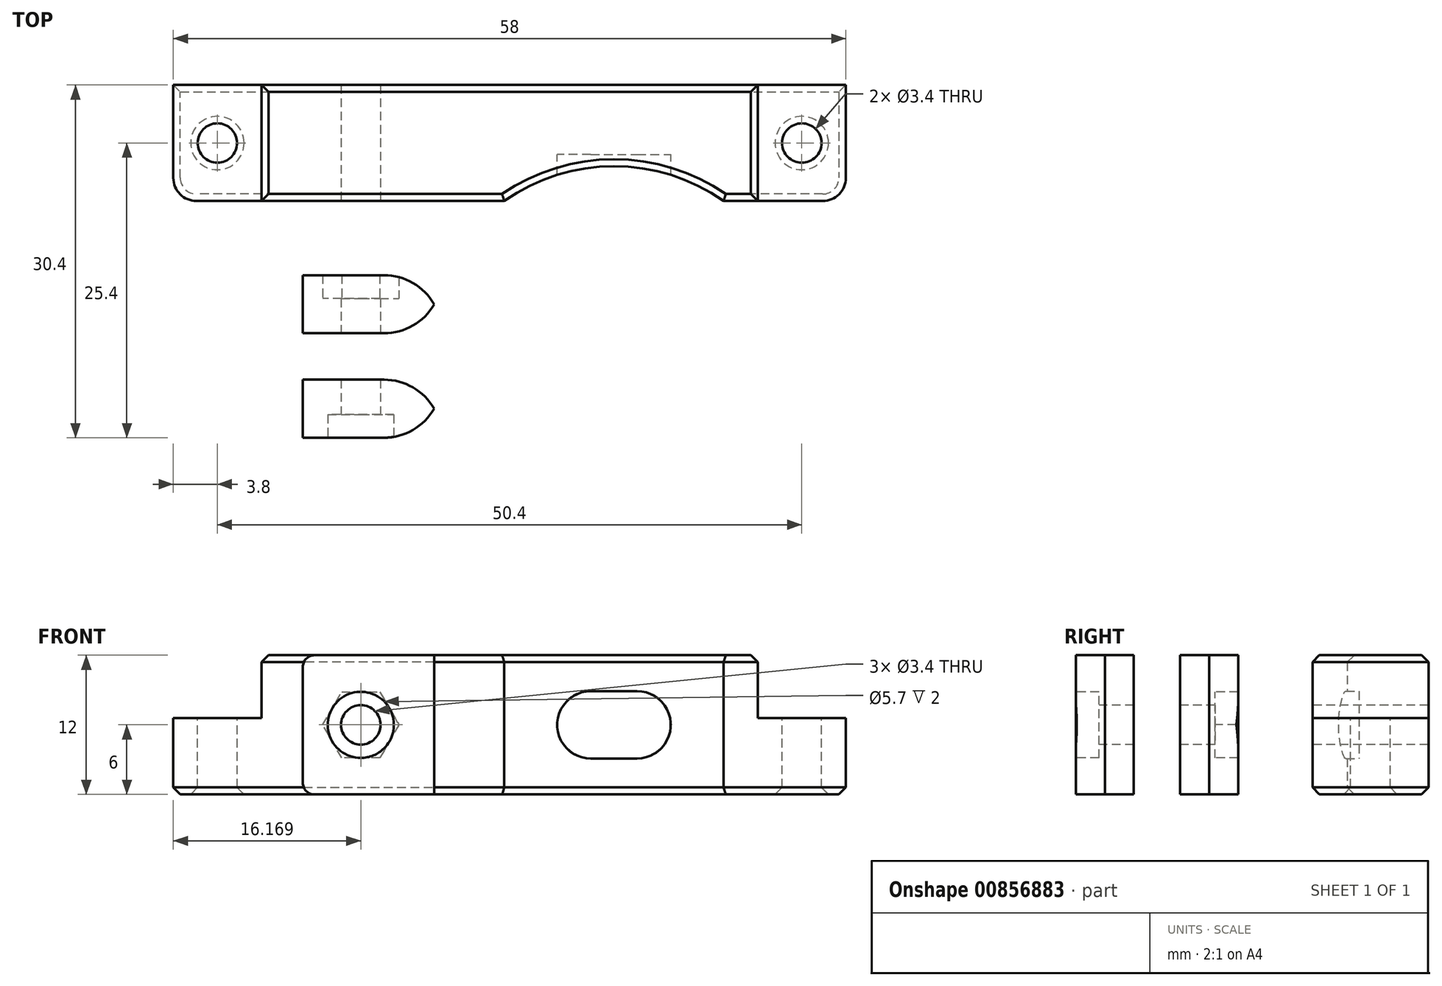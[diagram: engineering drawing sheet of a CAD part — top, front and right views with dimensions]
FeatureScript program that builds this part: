
annotation { "Feature Type Name" : "Feature", "Feature Type Description" : "" }
export const myFeature = defineFeature(function(context is Context, id is Id, definition is map)
    precondition{}
    {
        {
            var Q0;
            Q0=qCreatedBy(makeId("Top.planeOp"),FACE);
            var sketch = newSketch(context, id + "F0", { "sketchPlane" : qUnion([Q0])});
            skLineSegment(sketch, "E0.bottom", {"start": v(29, -5) * mm, "end": v(-29, -5) * mm});
            skLineSegment(sketch, "E0.top", {"start": v(29, 5) * mm, "end": v(-29, 5) * mm});
            skLineSegment(sketch, "E0.left", {"start": v(29, -5) * mm, "end": v(29, 5) * mm});
            skLineSegment(sketch, "E0.right", {"start": v(-29, -5) * mm, "end": v(-29, 5) * mm});
            skPoint(sketch, "E0.middle", {"position": v(0, 0) * mm});
            skCircle(sketch, "E1", {"center": v(9, -18.4) * mm, "radius": 13.4 * mm});
            skCircle(sketch, "E2", {"center": v(9, -18.4) * mm, "radius": 16.4 * mm});
            skLineSegment(sketch, "E3", {"start": v(-7.4, -18.4) * mm, "end": v(25.4, -18.4) * mm, "construction": true});
            skLineSegment(sketch, "E4", {"start": v(-7.28, -16.4) * mm, "end": v(-4.25, -16.4) * mm});
            skLineSegment(sketch, "E5.MirrorCS", {"start": v(-7.28, -20.4) * mm, "end": v(-4.25, -20.4) * mm});
            skLineSegment(sketch, "E6.bottom", {"start": v(-17.83, -16.4) * mm, "end": v(-5.83, -16.4) * mm});
            skLineSegment(sketch, "E6.top", {"start": v(-17.83, -11.4) * mm, "end": v(-5.83, -11.4) * mm});
            skLineSegment(sketch, "E6.left", {"start": v(-17.83, -16.4) * mm, "end": v(-17.83, -11.4) * mm});
            skLineSegment(sketch, "E6.right", {"start": v(-5.83, -16.4) * mm, "end": v(-5.83, -11.4) * mm});
            skLineSegment(sketch, "E7.MirrorCS", {"start": v(-17.83, -20.4) * mm, "end": v(-5.83, -20.4) * mm});
            skLineSegment(sketch, "E8.MirrorCS", {"start": v(-5.83, -20.4) * mm, "end": v(-5.83, -25.4) * mm});
            skLineSegment(sketch, "E9.MirrorCS", {"start": v(-17.83, -25.4) * mm, "end": v(-5.83, -25.4) * mm});
            skLineSegment(sketch, "E10.MirrorCS", {"start": v(-17.83, -20.4) * mm, "end": v(-17.83, -25.4) * mm});
            skSolve(sketch);
        }
        {
            var Q0;
            {var subQ5=sQuery(id+"F0.wireOp",EDGE,"E5.MirrorCS");Q0=makeQuery(id+"F0.imprint","IMPRINT",FACE,{"disambiguationData":[TD([[makeQuery(id+"F0.imprint","IMPRINT",EDGE,{"derivedFrom":subQ5}),-1.0]])]});}
            var Q1;
            {var subQ5=sQuery(id+"F0.wireOp",EDGE,"E4");Q1=makeQuery(id+"F0.imprint","IMPRINT",FACE,{"disambiguationData":[TD([[makeQuery(id+"F0.imprint","IMPRINT",EDGE,{"derivedFrom":subQ5}),1.0]])]});}
            var Q2;
            {var subQ0=sQuery(id+"F0.wireOp",EDGE,"E2");var subQ1=sQuery(id+"F0.wireOp",EDGE,"E0.bottom");var subQ2=makeQuery(id+"F0.imprint","INTERSECT",VERTEX,{"disambiguationData":[OD(0.0)],"derivedFrom":[subQ1,subQ0]});Q2=makeQuery(id+"F0.imprint","IMPRINT",FACE,{"disambiguationData":[TD([[makeQuery(id+"F0.imprint","IMPRINT",EDGE,{"disambiguationData":[TD([[subQ2,-1.0]])],"derivedFrom":subQ1}),-1.0]])]});}
            var Q3;
            Q3=makeQuery(id+"F0.imprint","IMPRINT",FACE,{"disambiguationData":[TD([[makeQuery(id+"F0.imprint","IMPRINT",EDGE,{"derivedFrom":sQuery(id+"F0.wireOp",EDGE,"E0.top")}),1.0]])]});
            var Q4;
            {var subQ0=sQuery(id+"F0.wireOp",EDGE,"E6.top");Q4=makeQuery(id+"F0.imprint","IMPRINT",FACE,{"disambiguationData":[TD([[makeQuery(id+"F0.imprint","IMPRINT",EDGE,{"derivedFrom":subQ0}),-1.0]])]});}
            var Q5;
            {var subQ0=sQuery(id+"F0.wireOp",EDGE,"E6.right");Q5=makeQuery(id+"F0.imprint","IMPRINT",FACE,{"disambiguationData":[TD([[makeQuery(id+"F0.imprint","IMPRINT",EDGE,{"derivedFrom":subQ0}),1.0]])]});}
            var Q6;
            {var subQ0=sQuery(id+"F0.wireOp",EDGE,"E9.MirrorCS");Q6=makeQuery(id+"F0.imprint","IMPRINT",FACE,{"disambiguationData":[TD([[makeQuery(id+"F0.imprint","IMPRINT",EDGE,{"derivedFrom":subQ0}),1.0]])]});}
            var Q7;
            {var subQ0=sQuery(id+"F0.wireOp",EDGE,"E8.MirrorCS");Q7=makeQuery(id+"F0.imprint","IMPRINT",FACE,{"disambiguationData":[TD([[makeQuery(id+"F0.imprint","IMPRINT",EDGE,{"derivedFrom":subQ0}),-1.0]])]});}
            extrude(context, id + "F1", {"entities" : qUnion([Q0, Q1, Q2, Q3, Q4, Q5, Q6, Q7]), "depth" : 12 * mm, "offsetDistance" : 25 * mm});
        }
        {
            var Q0;
            Q0=makeQuery(id+"F1.opExtrude","CAP_FACE",FACE,{"disambiguationData":[OSD([sQuery(id+"F0.wireOp",EDGE,"E0.bottom"),sQuery(id+"F0.wireOp",EDGE,"E0.top"),sQuery(id+"F0.wireOp",EDGE,"E0.left"),sQuery(id+"F0.wireOp",EDGE,"E0.right"),sQuery(id+"F0.wireOp",EDGE,"E1"),sQuery(id+"F0.wireOp",EDGE,"E2"),sQuery(id+"F0.wireOp",EDGE,"E4"),sQuery(id+"F0.wireOp",EDGE,"E5.MirrorCS"),sQuery(id+"F0.wireOp",EDGE,"E6.bottom"),sQuery(id+"F0.wireOp",EDGE,"E6.top"),sQuery(id+"F0.wireOp",EDGE,"E6.left"),sQuery(id+"F0.wireOp",EDGE,"E7.MirrorCS"),sQuery(id+"F0.wireOp",EDGE,"E9.MirrorCS"),sQuery(id+"F0.wireOp",EDGE,"E10.MirrorCS")])],"isStart":false});
            var sketch = newSketch(context, id + "F2", { "sketchPlane" : qUnion([Q0])});
            skCircle(sketch, "E11", {"center": v(-25.2, 0) * mm, "radius": 1.7 * mm});
            skCircle(sketch, "E12", {"center": v(25.2, 0) * mm, "radius": 1.7 * mm});
            skSolve(sketch);
        }
        {
            var Q0;
            Q0 = qSketchRegion(id + "F2", true);
            extrude(context, id + "F3", {"entities" : qUnion([Q0]), "operationType" : NewBodyOperationType.REMOVE, "endBound" : BoundingType.THROUGH_ALL, "oppositeDirection" : true, "depth" : 25 * mm, "offsetDistance" : 25 * mm});
        }
        {
            var Q0;
            Q0=makeQuery(id+"F1.opExtrude","SWEPT_FACE",FACE,{"disambiguationData":[OSD([sQuery(id+"F0.wireOp",EDGE,"E9.MirrorCS")])]});
            var sketch = newSketch(context, id + "F4", { "sketchPlane" : qUnion([Q0])});
            skCircle(sketch, "E13", {"center": v(-12.83, 6) * mm, "radius": 1.7 * mm});
            skPoint(sketch, "E14", {"position": v(-17.83, 6) * mm});
            skCircle(sketch, "E15.cCircle", {"center": v(-12.83, 6) * mm, "radius": 2.85 * mm});
            skLineSegment(sketch, "E15.0", {"start": v(-9.54, 6) * mm, "end": v(-11.19, 3.15) * mm});
            skLineSegment(sketch, "E15.1", {"start": v(-11.19, 3.15) * mm, "end": v(-14.48, 3.15) * mm});
            skLineSegment(sketch, "E15.2", {"start": v(-14.48, 3.15) * mm, "end": v(-16.12, 6) * mm});
            skLineSegment(sketch, "E15.3", {"start": v(-16.12, 6) * mm, "end": v(-14.48, 8.85) * mm});
            skLineSegment(sketch, "E15.4", {"start": v(-14.48, 8.85) * mm, "end": v(-11.19, 8.85) * mm});
            skLineSegment(sketch, "E15.5", {"start": v(-11.19, 8.85) * mm, "end": v(-9.54, 6) * mm});
            skPoint(sketch, "E15.0.midPoint", {"position": v(-10.36, 4.58) * mm});
            skSolve(sketch);
        }
        {
            var Q0;
            Q0=makeQuery(id+"F4.imprint","IMPRINT",FACE,{"disambiguationData":[TD([[makeQuery(id+"F4.imprint","IMPRINT",EDGE,{"derivedFrom":sQuery(id+"F4.wireOp",EDGE,"E13")}),1.0]])]});
            extrude(context, id + "F5", {"entities" : qUnion([Q0]), "operationType" : NewBodyOperationType.REMOVE, "endBound" : BoundingType.THROUGH_ALL, "oppositeDirection" : true, "depth" : 25 * mm, "offsetDistance" : 25 * mm});
        }
        {
            var Q0;
            Q0=makeQuery(id+"F4.imprint","IMPRINT",FACE,{"disambiguationData":[TD([[makeQuery(id+"F4.imprint","IMPRINT",EDGE,{"derivedFrom":sQuery(id+"F4.wireOp",EDGE,"E13")}),-1.0]])]});
            var Q1;
            {var subQ0=sQuery(id+"F4.wireOp",EDGE,"E15.3");var subQ1=sQuery(id+"F4.wireOp",EDGE,"E15.cCircle");var subQ2=makeQuery(id+"F4.imprint","INTERSECT",VERTEX,{"derivedFrom":[subQ1,subQ0]});Q1=makeQuery(id+"F4.imprint","IMPRINT",FACE,{"disambiguationData":[TD([[makeQuery(id+"F4.imprint","IMPRINT",EDGE,{"disambiguationData":[TD([[subQ2,-1.0]])],"derivedFrom":subQ1}),-1.0]])]});}
            var Q2;
            {var subQ0=sQuery(id+"F4.wireOp",EDGE,"E15.2");var subQ1=sQuery(id+"F4.wireOp",EDGE,"E15.cCircle");var subQ2=makeQuery(id+"F4.imprint","INTERSECT",VERTEX,{"derivedFrom":[subQ1,subQ0]});Q2=makeQuery(id+"F4.imprint","IMPRINT",FACE,{"disambiguationData":[TD([[makeQuery(id+"F4.imprint","IMPRINT",EDGE,{"disambiguationData":[TD([[subQ2,-1.0]])],"derivedFrom":subQ1}),-1.0]])]});}
            var Q3;
            {var subQ0=sQuery(id+"F4.wireOp",EDGE,"E15.1");var subQ1=sQuery(id+"F4.wireOp",EDGE,"E15.cCircle");var subQ2=makeQuery(id+"F4.imprint","INTERSECT",VERTEX,{"derivedFrom":[subQ1,subQ0]});Q3=makeQuery(id+"F4.imprint","IMPRINT",FACE,{"disambiguationData":[TD([[makeQuery(id+"F4.imprint","IMPRINT",EDGE,{"disambiguationData":[TD([[subQ2,-1.0]])],"derivedFrom":subQ1}),-1.0]])]});}
            var Q4;
            {var subQ0=sQuery(id+"F4.wireOp",EDGE,"E15.5");var subQ1=sQuery(id+"F4.wireOp",EDGE,"E15.cCircle");var subQ2=makeQuery(id+"F4.imprint","INTERSECT",VERTEX,{"derivedFrom":[subQ1,subQ0]});Q4=makeQuery(id+"F4.imprint","IMPRINT",FACE,{"disambiguationData":[TD([[makeQuery(id+"F4.imprint","IMPRINT",EDGE,{"disambiguationData":[TD([[subQ2,1.0]])],"derivedFrom":subQ1}),-1.0]])]});}
            var Q5;
            {var subQ0=sQuery(id+"F4.wireOp",EDGE,"E15.4");var subQ1=sQuery(id+"F4.wireOp",EDGE,"E15.cCircle");var subQ2=makeQuery(id+"F4.imprint","INTERSECT",VERTEX,{"derivedFrom":[subQ1,subQ0]});Q5=makeQuery(id+"F4.imprint","IMPRINT",FACE,{"disambiguationData":[TD([[makeQuery(id+"F4.imprint","IMPRINT",EDGE,{"disambiguationData":[TD([[subQ2,1.0]])],"derivedFrom":subQ1}),-1.0]])]});}
            var Q6;
            {var subQ0=sQuery(id+"F4.wireOp",EDGE,"E15.4");var subQ1=sQuery(id+"F4.wireOp",EDGE,"E15.cCircle");var subQ2=makeQuery(id+"F4.imprint","INTERSECT",VERTEX,{"derivedFrom":[subQ1,subQ0]});Q6=makeQuery(id+"F4.imprint","IMPRINT",FACE,{"disambiguationData":[TD([[makeQuery(id+"F4.imprint","IMPRINT",EDGE,{"disambiguationData":[TD([[subQ2,-1.0]])],"derivedFrom":subQ1}),-1.0]])]});}
            var Q7;
            Q7=makeQuery(id+"F1.opExtrude","SWEPT_FACE",FACE,{"disambiguationData":[OSD([sQuery(id+"F0.wireOp",EDGE,"E6.top")])]});
            var Q8;
            Q8=makeQuery(id+"F1.opExtrude","SWEPT_FACE",FACE,{"disambiguationData":[OSD([sQuery(id+"F0.wireOp",EDGE,"E4"),sQuery(id+"F0.wireOp",EDGE,"E6.bottom")])]});
            extrude(context, id + "F6", {"entities" : qUnion([Q0, Q1, Q2, Q3, Q4, Q5, Q6]), "operationType" : NewBodyOperationType.REMOVE, "endBound" : BoundingType.UP_TO_SURFACE, "oppositeDirection" : true, "depth" : 13.7 * mm, "endBoundEntityFace" : qUnion([Q7]), "offsetDistance" : 25 * mm, "hasSecondDirection" : true, "secondDirectionBound" : SecondDirectionBoundingType.UP_TO_SURFACE, "secondDirectionOppositeDirection" : true, "secondDirectionDepth" : 11.5 * mm, "secondDirectionBoundEntityFace" : qUnion([Q8]), "hasSecondDirectionOffset" : true, "secondDirectionOffsetDistance" : -3 * mm});
        }
        {
            var Q0;
            Q0=makeQuery(id+"F4.imprint","IMPRINT",FACE,{"disambiguationData":[TD([[makeQuery(id+"F4.imprint","IMPRINT",EDGE,{"derivedFrom":sQuery(id+"F4.wireOp",EDGE,"E13")}),-1.0]])]});
            extrude(context, id + "F7", {"entities" : qUnion([Q0]), "operationType" : NewBodyOperationType.REMOVE, "oppositeDirection" : true, "depth" : 2 * mm, "offsetDistance" : 25 * mm});
        }
        {
            var Q0;
            Q0=makeQuery(id+"F1.opExtrude","SWEPT_EDGE",EDGE,{"disambiguationData":[OSD([sQuery(id+"F0.wireOp",EDGE,"E1"),sQuery(id+"F0.wireOp",EDGE,"E4")])]});
            var Q1;
            Q1=makeQuery(id+"F1.opExtrude","SWEPT_EDGE",EDGE,{"disambiguationData":[OSD([sQuery(id+"F0.wireOp",EDGE,"E1"),sQuery(id+"F0.wireOp",EDGE,"E5.MirrorCS")])]});
            var Q2;
            Q2=makeQuery(id+"F1.opExtrude","SWEPT_EDGE",EDGE,{"disambiguationData":[OSD([sQuery(id+"F0.wireOp",EDGE,"E2"),sQuery(id+"F0.wireOp",EDGE,"E6.top"),sQuery(id+"F0.wireOp",EDGE,"E6.right")])]});
            var Q3;
            Q3=makeQuery(id+"F1.opExtrude","SWEPT_EDGE",EDGE,{"disambiguationData":[OSD([sQuery(id+"F0.wireOp",EDGE,"E2"),sQuery(id+"F0.wireOp",EDGE,"E8.MirrorCS"),sQuery(id+"F0.wireOp",EDGE,"E9.MirrorCS")])]});
            fillet(context, id + "F8", {"entities" : qUnion([Q0, Q1, Q2, Q3]), "radius" : 5 * mm, "tangentPropagation" : true, "allowEdgeOverflow" : false});
        }
        {
            var Q0;
            Q0=makeQuery(id+"F1.opExtrude","SWEPT_EDGE",EDGE,{"disambiguationData":[OSD([sQuery(id+"F0.wireOp",EDGE,"E0.bottom"),sQuery(id+"F0.wireOp",EDGE,"E0.right")])]});
            var Q1;
            Q1=makeQuery(id+"F1.opExtrude","SWEPT_EDGE",EDGE,{"disambiguationData":[OSD([sQuery(id+"F0.wireOp",EDGE,"E0.bottom"),sQuery(id+"F0.wireOp",EDGE,"E0.left")])]});
            fillet(context, id + "F9", {"entities" : qUnion([Q0, Q1]), "radius" : 2 * mm, "tangentPropagation" : true, "allowEdgeOverflow" : false});
        }
        {
            var Q0;
            Q0=makeQuery(id+"F1.opExtrude","CAP_FACE",FACE,{"disambiguationData":[OSD([sQuery(id+"F0.wireOp",EDGE,"E0.bottom"),sQuery(id+"F0.wireOp",EDGE,"E0.top"),sQuery(id+"F0.wireOp",EDGE,"E0.left"),sQuery(id+"F0.wireOp",EDGE,"E0.right"),sQuery(id+"F0.wireOp",EDGE,"E1"),sQuery(id+"F0.wireOp",EDGE,"E2"),sQuery(id+"F0.wireOp",EDGE,"E4"),sQuery(id+"F0.wireOp",EDGE,"E5.MirrorCS"),sQuery(id+"F0.wireOp",EDGE,"E6.bottom"),sQuery(id+"F0.wireOp",EDGE,"E6.top"),sQuery(id+"F0.wireOp",EDGE,"E6.left"),sQuery(id+"F0.wireOp",EDGE,"E7.MirrorCS"),sQuery(id+"F0.wireOp",EDGE,"E9.MirrorCS"),sQuery(id+"F0.wireOp",EDGE,"E10.MirrorCS")])],"isStart":false});
            var sketch = newSketch(context, id + "F10", { "sketchPlane" : qUnion([Q0])});
            skLineSegment(sketch, "E16.bottom", {"start": v(-29, 5) * mm, "end": v(-21.4, 5) * mm});
            skLineSegment(sketch, "E16.top", {"start": v(-29, -5) * mm, "end": v(-21.4, -5) * mm});
            skLineSegment(sketch, "E16.left", {"start": v(-29, 5) * mm, "end": v(-29, -5) * mm});
            skLineSegment(sketch, "E16.right", {"start": v(-21.4, 5) * mm, "end": v(-21.4, -5) * mm});
            skPoint(sketch, "E16.middle", {"position": v(-25.2, 0) * mm});
            skLineSegment(sketch, "E17.bottom", {"start": v(29, 5) * mm, "end": v(21.4, 5) * mm});
            skLineSegment(sketch, "E17.top", {"start": v(29, -5) * mm, "end": v(21.4, -5) * mm});
            skLineSegment(sketch, "E17.left", {"start": v(29, 5) * mm, "end": v(29, -5) * mm});
            skLineSegment(sketch, "E17.right", {"start": v(21.4, 5) * mm, "end": v(21.4, -5) * mm});
            skPoint(sketch, "E17.middle", {"position": v(25.2, 0) * mm});
            skSolve(sketch);
        }
        {
            var Q0;
            {var subQ1=sQuery(id+"F10.wireOp",EDGE,"E16.bottom");Q0=makeQuery(id+"F10.imprint","IMPRINT",FACE,{"disambiguationData":[TD([[makeQuery(id+"F10.imprint","IMPRINT",EDGE,{"derivedFrom":subQ1}),1.0]])]});}
            var Q1;
            {var subQ1=sQuery(id+"F10.wireOp",EDGE,"E17.bottom");Q1=makeQuery(id+"F10.imprint","IMPRINT",FACE,{"disambiguationData":[TD([[makeQuery(id+"F10.imprint","IMPRINT",EDGE,{"derivedFrom":subQ1}),1.0]])]});}
            extrude(context, id + "F11", {"entities" : qUnion([Q0, Q1]), "operationType" : NewBodyOperationType.REMOVE, "oppositeDirection" : true, "depth" : 5.4 * mm, "offsetDistance" : 25 * mm});
        }
        {
            var Q0;
            Q0=makeQuery(id+"F11.boolean.opBoolean","COPY",EDGE,{"derivedFrom":makeQuery(id+"F11.opExtrude","CAP_EDGE",EDGE,{"disambiguationData":[OSD([sQuery(id+"F10.wireOp",EDGE,"E17.right")])],"isStart":true})});
            var Q1;
            Q1=makeQuery(id+"F11.boolean.opBoolean","COPY",EDGE,{"derivedFrom":makeQuery(id+"F11.opExtrude","CAP_EDGE",EDGE,{"disambiguationData":[OSD([sQuery(id+"F10.wireOp",EDGE,"E16.right")])],"isStart":true})});
            var Q2;
            Q2=makeQuery(id+"F1.opExtrude","CAP_EDGE",EDGE,{"disambiguationData":[OSD([sQuery(id+"F0.wireOp",EDGE,"E6.left")])],"isStart":true});
            var Q3;
            Q3=makeQuery(id+"F1.opExtrude","CAP_EDGE",EDGE,{"disambiguationData":[OSD([sQuery(id+"F0.wireOp",EDGE,"E10.MirrorCS")])],"isStart":true});
            var Q4;
            Q4=makeQuery(id+"F1.opExtrude","CAP_EDGE",EDGE,{"disambiguationData":[OSD([sQuery(id+"F0.wireOp",EDGE,"E10.MirrorCS")])],"isStart":false});
            var Q5;
            Q5=makeQuery(id+"F1.opExtrude","CAP_EDGE",EDGE,{"disambiguationData":[OSD([sQuery(id+"F0.wireOp",EDGE,"E6.left")])],"isStart":false});
            fillet(context, id + "F12", {"entities" : qUnion([Q0, Q1, Q2, Q3, Q4, Q5]), "radius" : 1 * mm, "tangentPropagation" : true, "allowEdgeOverflow" : false});
        }
        {
            var Q0;
            Q0=makeQuery(id+"F1.opExtrude","CAP_FACE",FACE,{"disambiguationData":[OSD([sQuery(id+"F0.wireOp",EDGE,"E0.bottom"),sQuery(id+"F0.wireOp",EDGE,"E0.top"),sQuery(id+"F0.wireOp",EDGE,"E0.left"),sQuery(id+"F0.wireOp",EDGE,"E0.right"),sQuery(id+"F0.wireOp",EDGE,"E1"),sQuery(id+"F0.wireOp",EDGE,"E2"),sQuery(id+"F0.wireOp",EDGE,"E4"),sQuery(id+"F0.wireOp",EDGE,"E5.MirrorCS"),sQuery(id+"F0.wireOp",EDGE,"E6.bottom"),sQuery(id+"F0.wireOp",EDGE,"E6.top"),sQuery(id+"F0.wireOp",EDGE,"E6.left"),sQuery(id+"F0.wireOp",EDGE,"E7.MirrorCS"),sQuery(id+"F0.wireOp",EDGE,"E9.MirrorCS"),sQuery(id+"F0.wireOp",EDGE,"E10.MirrorCS")])],"isStart":true});
            var Q1;
            Q1=makeQuery(id+"F1.opExtrude","CAP_FACE",FACE,{"disambiguationData":[OSD([sQuery(id+"F0.wireOp",EDGE,"E0.bottom"),sQuery(id+"F0.wireOp",EDGE,"E0.top"),sQuery(id+"F0.wireOp",EDGE,"E0.left"),sQuery(id+"F0.wireOp",EDGE,"E0.right"),sQuery(id+"F0.wireOp",EDGE,"E1"),sQuery(id+"F0.wireOp",EDGE,"E2"),sQuery(id+"F0.wireOp",EDGE,"E4"),sQuery(id+"F0.wireOp",EDGE,"E5.MirrorCS"),sQuery(id+"F0.wireOp",EDGE,"E6.bottom"),sQuery(id+"F0.wireOp",EDGE,"E6.top"),sQuery(id+"F0.wireOp",EDGE,"E6.left"),sQuery(id+"F0.wireOp",EDGE,"E7.MirrorCS"),sQuery(id+"F0.wireOp",EDGE,"E9.MirrorCS"),sQuery(id+"F0.wireOp",EDGE,"E10.MirrorCS")])],"isStart":false});
            chamfer(context, id + "F13", {"entities" : qUnion([Q0, Q1]), "width" : .6 * mm, "tangentPropagation" : true});
        }
        {
            var Q0;
            Q0=qCreatedBy(makeId("Front.planeOp"),FACE);
            var sketch = newSketch(context, id + "F14", { "sketchPlane" : qUnion([Q0])});
            skLineSegment(sketch, "E18", {"start": v(7, 6) * mm, "end": v(11, 6) * mm, "construction": true});
            skArc(sketch, "E19.0.startCap", {"start": v(7, 3.1) * mm, "mid": v(4.1, 6) * mm, "end": v(7, 8.9) * mm});
            skArc(sketch, "E19.0.endCap", {"start": v(11, 8.9) * mm, "mid": v(13.9, 6) * mm, "end": v(11, 3.1) * mm});
            skLineSegment(sketch, "E19.0.left", {"start": v(7, 8.9) * mm, "end": v(11, 8.9) * mm});
            skLineSegment(sketch, "E19.0.right", {"start": v(7, 3.1) * mm, "end": v(11, 3.1) * mm});
            skLineSegment(sketch, "E20", {"start": v(-4.58, 6) * mm, "end": v(29, 6) * mm, "construction": true});
            skSolve(sketch);
        }
        {
            var Q0;
            Q0 = qSketchRegion(id + "F14", true);
            extrude(context, id + "F15", {"entities" : qUnion([Q0]), "operationType" : NewBodyOperationType.REMOVE, "endBound" : BoundingType.THROUGH_ALL, "depth" : 51.6 * mm, "offsetDistance" : 25 * mm, "hasSecondDirection" : true, "secondDirectionOppositeDirection" : false, "secondDirectionDepth" : 1 * mm});
        }
    });
